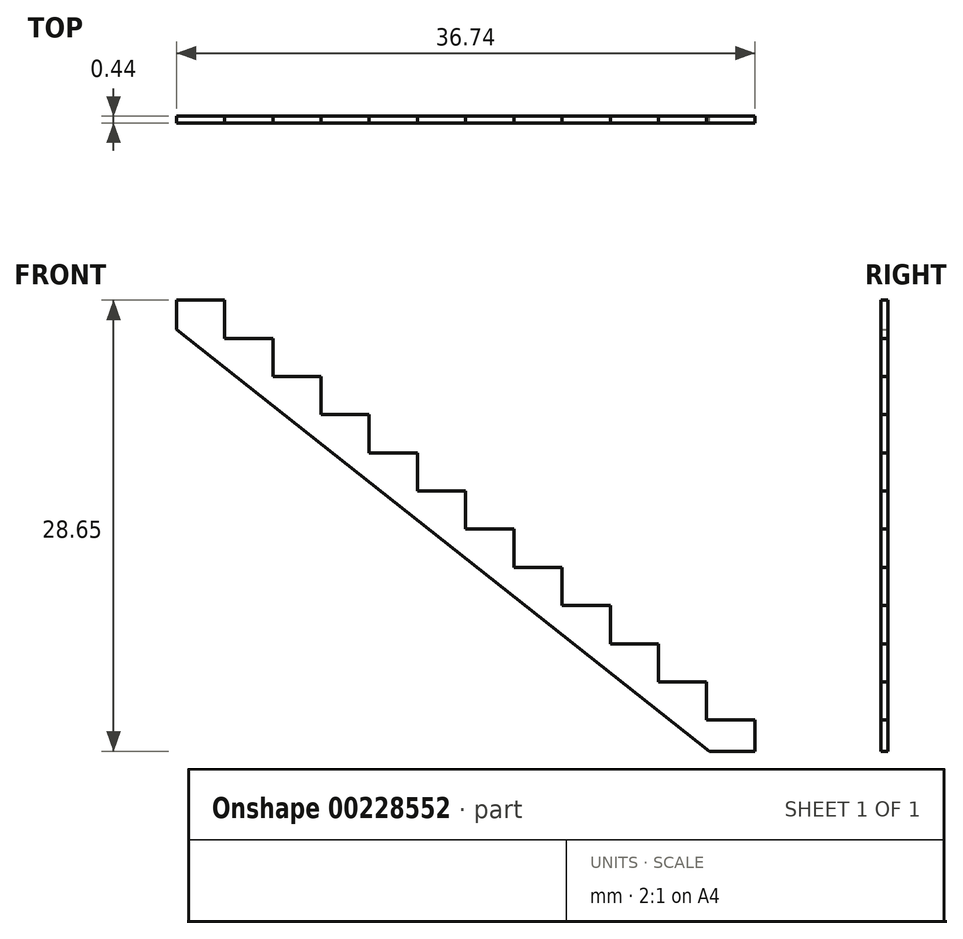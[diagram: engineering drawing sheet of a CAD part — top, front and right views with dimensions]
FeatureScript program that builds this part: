
annotation { "Feature Type Name" : "Feature", "Feature Type Description" : "" }
export const myFeature = defineFeature(function(context is Context, id is Id, definition is map)
    precondition{}
    {
        {
            var Q0;
            Q0=qCreatedBy(makeId("Front.planeOp"),FACE);
            var sketch = newSketch(context, id + "F0", { "sketchPlane" : qUnion([Q0])});
            skLineSegment(sketch, "E0", {"start": v(0, 0) * mm, "end": v(0, 173.04) * mm});
            skLineSegment(sketch, "E1", {"start": v(0, 173.04) * mm, "end": v(-266.7, 173.04) * mm});
            skLineSegment(sketch, "E2", {"start": v(-266.7, 173.04) * mm, "end": v(-266.7, 384.18) * mm});
            skLineSegment(sketch, "E3", {"start": v(-266.7, 384.18) * mm, "end": v(-533.4, 384.18) * mm});
            skLineSegment(sketch, "E4", {"start": v(-533.4, 384.18) * mm, "end": v(-533.4, 595.31) * mm});
            skLineSegment(sketch, "E5", {"start": v(-533.4, 595.31) * mm, "end": v(-800.1, 595.31) * mm});
            skLineSegment(sketch, "E6", {"start": v(-800.1, 595.31) * mm, "end": v(-800.1, 806.45) * mm});
            skLineSegment(sketch, "E7", {"start": v(-800.1, 806.45) * mm, "end": v(-1066.8, 806.45) * mm});
            skLineSegment(sketch, "E8", {"start": v(-1066.8, 806.45) * mm, "end": v(-1066.8, 1017.59) * mm});
            skLineSegment(sketch, "E9", {"start": v(-1066.8, 1017.59) * mm, "end": v(-1333.5, 1017.59) * mm});
            skLineSegment(sketch, "E10", {"start": v(-1333.5, 1017.59) * mm, "end": v(-1333.5, 1228.73) * mm});
            skLineSegment(sketch, "E11", {"start": v(-1333.5, 1228.73) * mm, "end": v(-1600.2, 1228.73) * mm});
            skLineSegment(sketch, "E12", {"start": v(-1600.2, 1228.73) * mm, "end": v(-1600.2, 1439.86) * mm});
            skLineSegment(sketch, "E13", {"start": v(-1600.2, 1439.86) * mm, "end": v(-1866.9, 1439.86) * mm});
            skLineSegment(sketch, "E14", {"start": v(-1866.9, 1651) * mm, "end": v(-2133.6, 1651) * mm});
            skLineSegment(sketch, "E15", {"start": v(-2133.6, 1651) * mm, "end": v(-2133.6, 1862.14) * mm});
            skLineSegment(sketch, "E16", {"start": v(-2133.6, 1862.14) * mm, "end": v(-2400.3, 1862.14) * mm});
            skLineSegment(sketch, "E17", {"start": v(-2400.3, 1862.14) * mm, "end": v(-2400.3, 2073.28) * mm});
            skLineSegment(sketch, "E18", {"start": v(-2400.3, 2073.28) * mm, "end": v(-2667, 2073.28) * mm});
            skLineSegment(sketch, "E19", {"start": v(-2667, 2073.28) * mm, "end": v(-2667, 2284.41) * mm});
            skLineSegment(sketch, "E20", {"start": v(-2667, 2284.41) * mm, "end": v(-2933.7, 2284.41) * mm});
            skLineSegment(sketch, "E21", {"start": v(-2933.7, 2284.41) * mm, "end": v(-2933.7, 2495.55) * mm});
            skLineSegment(sketch, "E22", {"start": v(-2933.7, 2495.55) * mm, "end": v(-3200.4, 2495.55) * mm});
            skLineSegment(sketch, "E23", {"start": v(-3200.4, 2334.13) * mm, "end": v(-3200.4, 2495.55) * mm});
            skLineSegment(sketch, "E24", {"start": v(-1866.9, 1439.86) * mm, "end": v(-1866.9, 1651) * mm});
            skLineSegment(sketch, "E25", {"start": v(-3200.4, 2334.13) * mm, "end": v(-252.02, 0) * mm});
            skLineSegment(sketch, "E26", {"start": v(-252.02, 0) * mm, "end": v(0, 0) * mm});
            skLineSegment(sketch, "E27", {"start": v(-2933.7, 2495.55) * mm, "end": v(-2133.6, 1862.14) * mm, "construction": true});
            skLineSegment(sketch, "E28", {"start": v(-1466.85, 1228.73) * mm, "end": v(-1466.85, 3057.53) * mm, "construction": true});
            skSolve(sketch);
        }
        {
            var Q0;
            Q0=makeQuery(id+"F0.imprint","IMPRINT",FACE,{"disambiguationData":[TD([[makeQuery(id+"F0.imprint","IMPRINT",EDGE,{"derivedFrom":sQuery(id+"F0.wireOp",EDGE,"E0")}),1.0]])]});
            extrude(context, id + "F1", {"entities" : qUnion([Q0]), "depth" : 38.1 * mm});
        }
        {
            var Q0;
            Q0=makeQuery(id+"F1.opExtrude","SWEPT_BODY",BODY,{"disambiguationData":[OSD([sQuery(id+"F0.wireOp",EDGE,"E0"),sQuery(id+"F0.wireOp",EDGE,"E1"),sQuery(id+"F0.wireOp",EDGE,"E2"),sQuery(id+"F0.wireOp",EDGE,"E3"),sQuery(id+"F0.wireOp",EDGE,"E4"),sQuery(id+"F0.wireOp",EDGE,"E5"),sQuery(id+"F0.wireOp",EDGE,"E6"),sQuery(id+"F0.wireOp",EDGE,"E7"),sQuery(id+"F0.wireOp",EDGE,"E8"),sQuery(id+"F0.wireOp",EDGE,"E9"),sQuery(id+"F0.wireOp",EDGE,"E10"),sQuery(id+"F0.wireOp",EDGE,"E11"),sQuery(id+"F0.wireOp",EDGE,"E12"),sQuery(id+"F0.wireOp",EDGE,"E13"),sQuery(id+"F0.wireOp",EDGE,"E14"),sQuery(id+"F0.wireOp",EDGE,"E15"),sQuery(id+"F0.wireOp",EDGE,"E16"),sQuery(id+"F0.wireOp",EDGE,"E17"),sQuery(id+"F0.wireOp",EDGE,"E18"),sQuery(id+"F0.wireOp",EDGE,"E19"),sQuery(id+"F0.wireOp",EDGE,"E20"),sQuery(id+"F0.wireOp",EDGE,"E21"),sQuery(id+"F0.wireOp",EDGE,"E22"),sQuery(id+"F0.wireOp",EDGE,"E23"),sQuery(id+"F0.wireOp",EDGE,"E24"),sQuery(id+"F0.wireOp",EDGE,"E25"),sQuery(id+"F0.wireOp",EDGE,"E26")])]});
            var Q1;
            Q1=qCreatedBy(makeId("Origin.pointOp"),VERTEX);
            transform(context, id + "F2", {"entities" : qUnion([Q0]), "transformType" : TransformType.SCALE_UNIFORMLY, "scale" : 1 / 87.1, "scalePoint" : qUnion([Q1]), "makeCopy" : false});
        }
    });
